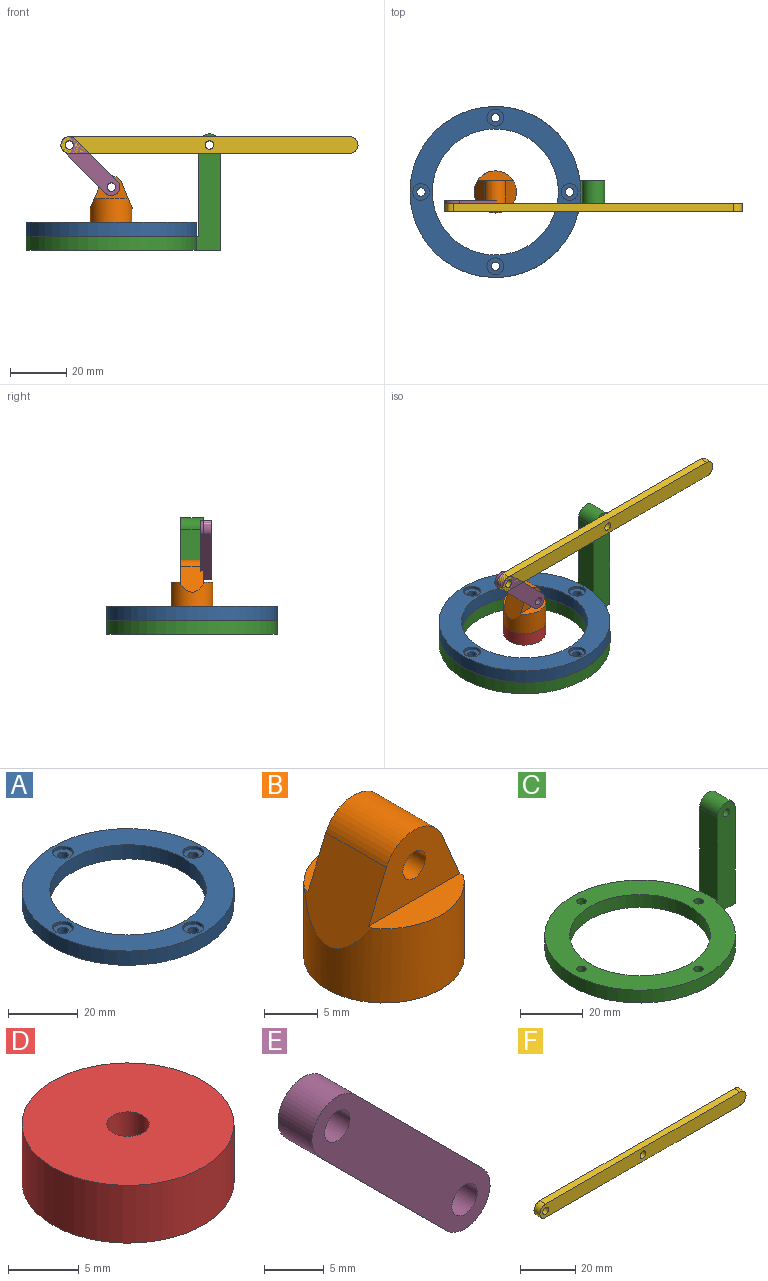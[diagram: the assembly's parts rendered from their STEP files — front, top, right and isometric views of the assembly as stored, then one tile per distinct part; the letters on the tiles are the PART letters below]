
ASSEMBLY  parts=6 mates=6
PART A: 16 faces, bbox 61x61x5 mm
  f0: cylinder r=3mm len=6mm, axis (0,0,-1), area 18.8mm2, adj f6,f9
  f1: cylinder r=3mm len=6mm, axis (0,0,-1), area 18.8mm2, adj f6,f11
  f2: cylinder r=3mm len=6mm, axis (0,0,-1), area 18.8mm2, adj f6,f13
  f3: cylinder r=3mm len=6mm, axis (0,0,-1), area 18.8mm2, adj f6,f15
  f4: cylinder r=22.5mm len=45mm, axis (0,0,-1), area 706.9mm2, adj f6,f7
  f5: cylinder r=30.5mm len=61mm, axis (0,0,-1), area 958.2mm2, adj f6,f7
  f6: plane 61x61mm, normal (0,0,1), area 1218.9mm2, adj f0,f1,f2,f3,f4,f5
  f7: plane 61x61mm, normal (0,0,-1), area 1303.8mm2, adj f4,f5,f8,f10,f12,f14
  f8: cylinder r=1.5mm len=4mm, axis (0,0,-1), area 37.7mm2, adj f7,f9
  f9: plane 6x6mm, normal (0,0,1), area 21.2mm2, adj f0,f8
  f10: cylinder r=1.5mm len=4mm, axis (0,0,-1), area 37.7mm2, adj f7,f11
  f11: plane 6x6mm, normal (0,0,1), area 21.2mm2, adj f1,f10
  f12: cylinder r=1.5mm len=4mm, axis (0,0,-1), area 37.7mm2, adj f7,f13
  f13: plane 6x6mm, normal (0,0,1), area 21.2mm2, adj f2,f12
  f14: cylinder r=1.5mm len=4mm, axis (0,0,-1), area 37.7mm2, adj f7,f15
  f15: plane 6x6mm, normal (0,0,1), area 21.2mm2, adj f3,f14
PART B: 12 faces, bbox 15x15x16.5 mm
  f0: plane 15x15mm, normal (0,0,-1), area 169.6mm2, adj f9,f10
  f1: plane 12.05x3.5mm, normal (0,0,1), area 31.2mm2, adj f2,f4,f7,f9
  f2: plane 9.05x8.93mm, normal (0.92,0,0.39), area 71.3mm2, adj f1,f3,f5,f7,f8,f9
  f3: plane 12.05x3.5mm, normal (0,0,1), area 31.2mm2, adj f2,f4,f8,f9
  f4: plane 9.05x8.93mm, normal (-0.92,0,0.39), area 71.3mm2, adj f1,f3,f5,f7,f8,f9
  f5: cylinder r=4mm len=8mm, axis (0,1,0), area 75mm2, adj f2,f4,f7,f8
  f6: cylinder r=1.5mm len=8mm, axis (0,1,0), area 75.4mm2, adj f7,f8
  f7: plane 12.05x8mm, normal (0,-1,0), area 59.9mm2, adj f1,f2,f4,f5,f6
  f8: plane 12.05x8mm, normal (0,1,0), area 59.9mm2, adj f2,f3,f4,f5,f6
  f9: cylinder r=7.5mm len=15mm, axis (0,0,-1), area 356.2mm2, adj f0,f1,f2,f3,f4
  f10: cylinder r=1.5mm len=3mm, axis (0,0,-1), area 28.3mm2, adj f0,f11
  f11: plane 3x3mm, normal (0,0,-1), area 7.1mm2, adj f10
PART C: 14 faces, bbox 69.5x61x41.5 mm
  f0: plane 41.5x8.76mm, normal (0,-1,0), area 321.9mm2, adj f1,f3,f4,f5,f6,f7,f13
  f1: plane 37.5x8mm, normal (1,0,0), area 300mm2, adj f0,f2,f4,f13
  f2: plane 41.5x8.76mm, normal (0,1,0), area 321.9mm2, adj f1,f3,f4,f5,f6,f7,f13
  f3: cylinder r=1.5mm len=8mm, axis (0,1,0), area 75.4mm2, adj f0,f2
  f4: cylinder r=4mm len=8mm, axis (0,1,0), area 100.5mm2, adj f0,f1,f2,f5
  f5: plane 32.5x8mm, normal (-1,0,0), area 260mm2, adj f0,f2,f4,f6
  f6: plane 61.5x61mm, normal (0,0,1), area 1308.5mm2, adj f0,f2,f5,f7,f8,f9,f10,f11
  f7: cylinder r=30.5mm len=61mm, axis (0,0,1), area 918.1mm2, adj f0,f2,f6,f13
  f8: cylinder r=1.5mm len=5mm, axis (0,0,1), area 47.1mm2, adj f6,f13
  f9: cylinder r=1.5mm len=5mm, axis (0,0,1), area 47.1mm2, adj f6,f13
  f10: cylinder r=1.5mm len=5mm, axis (0,0,1), area 47.1mm2, adj f6,f13
  f11: cylinder r=22.5mm len=45mm, axis (0,0,1), area 706.9mm2, adj f6,f13
  f12: cylinder r=1.5mm len=5mm, axis (0,0,1), area 47.1mm2, adj f6,f13
  f13: plane 69.5x61mm, normal (0,0,-1), area 1372.5mm2, adj f0,f1,f2,f7,f8,f9,f10,f11
PART D: 6 faces, bbox 15x15x5 mm
  f0: cylinder r=3mm len=6mm, axis (0,0,1), area 18.8mm2, adj f2,f5
  f1: cylinder r=7.5mm len=15mm, axis (0,0,1), area 235.6mm2, adj f2,f3
  f2: plane 15x15mm, normal (0,0,-1), area 148.4mm2, adj f0,f1
  f3: plane 15x15mm, normal (0,0,1), area 169.6mm2, adj f1,f4
  f4: cylinder r=1.5mm len=4mm, axis (0,0,1), area 37.7mm2, adj f3,f5
  f5: plane 6x6mm, normal (0,0,-1), area 21.2mm2, adj f0,f4
PART E: 8 faces, bbox 21x4x21 mm
  f0: cylinder r=3mm len=5.12mm, axis (0,1,0), area 37.7mm2, adj f1,f3,f6,f7
  f1: plane 15x15mm, normal (-0.71,0,-0.71), area 84.9mm2, adj f0,f2,f6,f7
  f2: cylinder r=3mm len=5.12mm, axis (0,1,0), area 37.7mm2, adj f1,f3,f6,f7
  f3: plane 15x15mm, normal (0.71,0,0.71), area 84.9mm2, adj f0,f2,f6,f7
  f4: cylinder r=1.5mm len=4mm, axis (0,1,0), area 37.7mm2, adj f6,f7
  f5: cylinder r=1.5mm len=4mm, axis (0,1,0), area 37.7mm2, adj f6,f7
  f6: plane 21x21mm, normal (0,-1,0), area 141.4mm2, adj f0,f1,f2,f3,f4,f5
  f7: plane 21x21mm, normal (0,1,0), area 141.4mm2, adj f0,f1,f2,f3,f4,f5
PART F: 8 faces, bbox 106x3x6 mm
  f0: cylinder r=3mm len=6mm, axis (0,1,0), area 28.3mm2, adj f1,f4,f6,f7
  f1: plane 100x3mm, normal (0,0,1), area 300mm2, adj f0,f2,f6,f7
  f2: cylinder r=3mm len=6mm, axis (0,1,0), area 28.3mm2, adj f1,f4,f6,f7
  f3: cylinder r=1.5mm len=3mm, axis (0,1,0), area 28.3mm2, adj f6,f7
  f4: plane 100x3mm, normal (0,0,-1), area 300mm2, adj f0,f2,f6,f7
  f5: cylinder r=1.5mm len=3mm, axis (0,1,0), area 28.3mm2, adj f6,f7
  f6: plane 106x6mm, normal (0,-1,0), area 614.1mm2, adj f0,f1,f2,f3,f4,f5
  f7: plane 106x6mm, normal (0,1,0), area 614.1mm2, adj f0,f1,f2,f3,f4,f5
PLACE A t=(-36.28,31.1,-8.25)mm
PLACE B t=(-36.28,31.1,-8.25)mm
PLACE C t=(-36.28,31.1,-8.25)mm fixed
PLACE D rot(axis=(1,0,0),180deg) t=(-36.28,31.1,-3.25)mm
PLACE E rot(axis=(0,1,0),0deg) t=(-36.28,32.1,-8.25)mm
PLACE F rot(axis=(0,1,0),0deg) t=(-36.28,31.1,-8.25)mm
MATE revolute F.f5 <-> C.f3  axis (0,1,0) through (-1.28,27.1,24.25)mm
MATE fastened A.f4 <-> C.f11  axis (0,0,-1) through (-36.28,31.1,-8.25)mm
MATE fastened B.f9 <-> D.f1  axis (0,0,-1) through (-36.28,31.1,-3.25)mm
MATE revolute E.f0 <-> F.f2  axis (0,-1,0) through (-51.28,24.1,24.25)mm
MATE slider A.f4 <-> D.f1  axis (0,0,1) through (-36.28,31.1,-3.25)mm
MATE cylindrical E.f5 <-> B.f6  axis (0,-1,0) through (-36.28,24.1,9.25)mm
